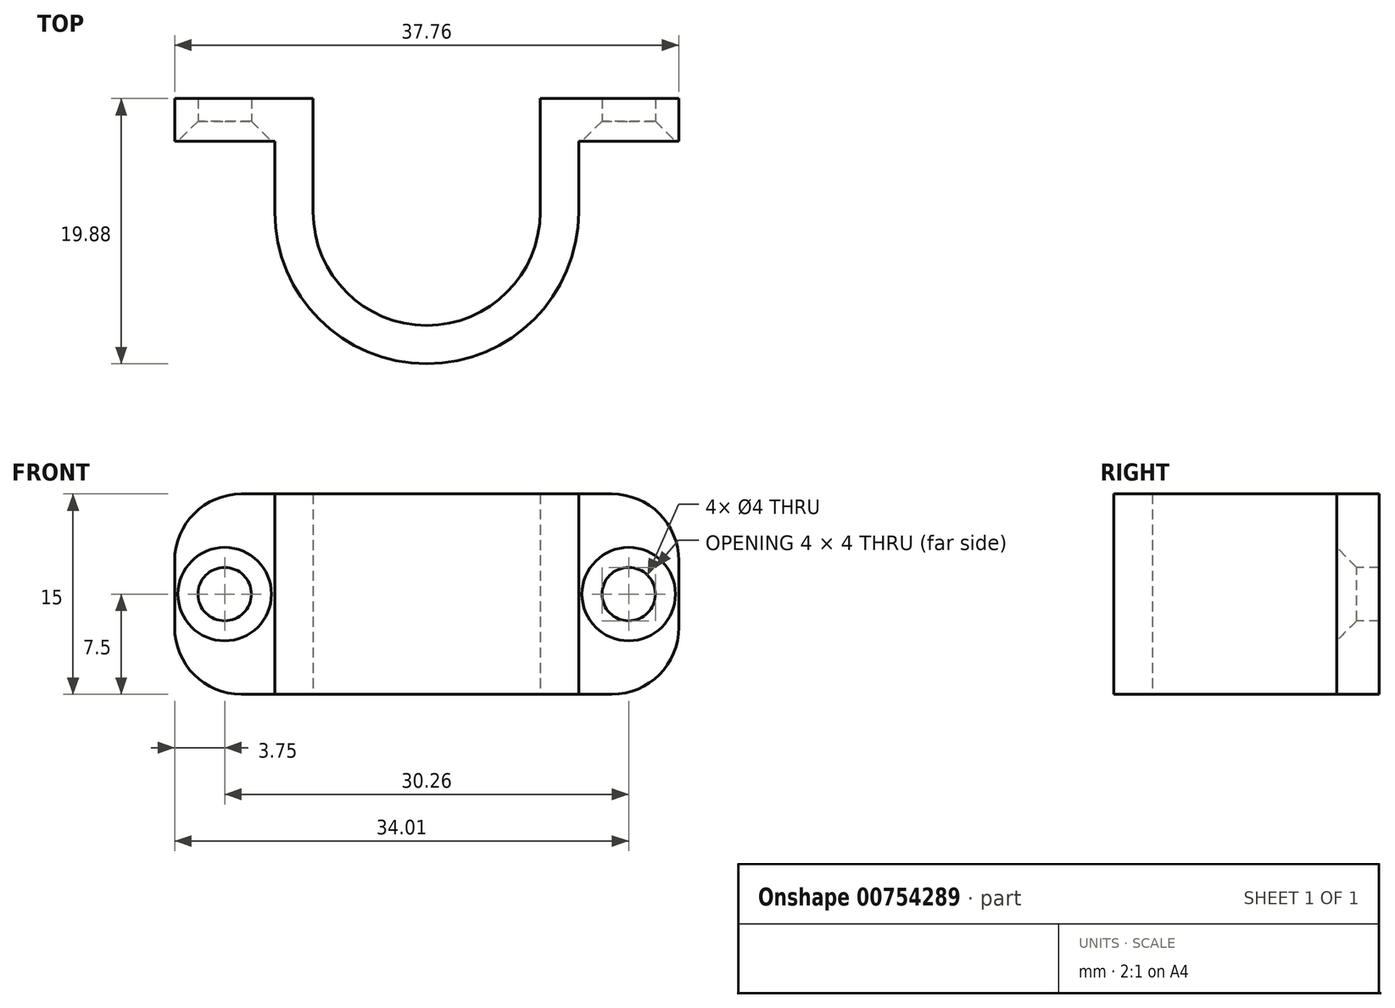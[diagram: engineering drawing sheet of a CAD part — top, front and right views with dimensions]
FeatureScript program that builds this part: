
annotation { "Feature Type Name" : "Feature", "Feature Type Description" : "" }
export const myFeature = defineFeature(function(context is Context, id is Id, definition is map)
    precondition{}
    {
        {
            var Q0;
            Q0=qCreatedBy(makeId("Top.planeOp"),FACE);
            var sketch = newSketch(context, id + "F0", { "sketchPlane" : qUnion([Q0])});
            skCircle(sketch, "E0", {"center": v(0, 0) * mm, "radius": 8.5 * mm});
            skLineSegment(sketch, "E1", {"start": v(-8.5, 0) * mm, "end": v(-8.5, 8.5) * mm});
            skLineSegment(sketch, "E2", {"start": v(-8.5, 8.5) * mm, "end": v(8.5, 8.5) * mm});
            skLineSegment(sketch, "E3", {"start": v(8.5, 8.5) * mm, "end": v(8.5, 0) * mm});
            skLineSegment(sketch, "E4.bottom", {"start": v(-8.5, 8.5) * mm, "end": v(-18.88, 8.5) * mm});
            skLineSegment(sketch, "E4.top", {"start": v(-8.5, 5.3) * mm, "end": v(-18.88, 5.3) * mm});
            skLineSegment(sketch, "E4.left", {"start": v(-8.5, 8.5) * mm, "end": v(-8.5, 5.3) * mm});
            skLineSegment(sketch, "E4.right", {"start": v(-18.88, 8.5) * mm, "end": v(-18.88, 5.3) * mm});
            skLineSegment(sketch, "E5", {"start": v(0, 0) * mm, "end": v(0, 27.69) * mm, "construction": true});
            skPoint(sketch, "E5.endSnap0", {"position": v(0, 8.5) * mm});
            skLineSegment(sketch, "E6.MirrorCS", {"start": v(8.5, 8.5) * mm, "end": v(8.5, 5.3) * mm});
            skLineSegment(sketch, "E7.MirrorCS", {"start": v(8.5, 5.3) * mm, "end": v(18.88, 5.3) * mm});
            skLineSegment(sketch, "E8.MirrorCS", {"start": v(8.5, 8.5) * mm, "end": v(18.88, 8.5) * mm});
            skLineSegment(sketch, "E9.MirrorCS", {"start": v(18.88, 8.5) * mm, "end": v(18.88, 5.3) * mm});
            skCircle(sketch, "E10", {"center": v(0, 0) * mm, "radius": 11.38 * mm});
            skLineSegment(sketch, "E11", {"start": v(-11.38, 0) * mm, "end": v(-11.38, 5.3) * mm});
            skLineSegment(sketch, "E12.MirrorCS", {"start": v(11.38, 0) * mm, "end": v(11.38, 5.3) * mm});
            skLineSegment(sketch, "E13", {"start": v(-8.5, 5.3) * mm, "end": v(8.5, 5.3) * mm});
            skSolve(sketch);
        }
        {
            var Q0;
            {var subQ4=sQuery(id+"F0.wireOp",EDGE,"E4.bottom");Q0=makeQuery(id+"F0.imprint","IMPRINT",FACE,{"disambiguationData":[TD([[makeQuery(id+"F0.imprint","IMPRINT",EDGE,{"derivedFrom":subQ4}),1.0]])]});}
            var Q1;
            {var subQ0=sQuery(id+"F0.wireOp",EDGE,"E11");Q1=makeQuery(id+"F0.imprint","IMPRINT",FACE,{"disambiguationData":[TD([[makeQuery(id+"F0.imprint","IMPRINT",EDGE,{"derivedFrom":subQ0}),-1.0]])]});}
            var Q2;
            {var subQ2=sQuery(id+"F0.wireOp",EDGE,"E1");var subQ9=sQuery(id+"F0.wireOp",EDGE,"E0");var subQ11=makeQuery(id+"F0.imprint","INTERSECT",VERTEX,{"derivedFrom":[subQ9,subQ2]});Q2=makeQuery(id+"F0.imprint","IMPRINT",FACE,{"disambiguationData":[TD([[makeQuery(id+"F0.imprint","IMPRINT",EDGE,{"disambiguationData":[TD([[subQ11,-1.0]])],"derivedFrom":subQ9}),-1.0]])]});}
            var Q3;
            {var subQ0=sQuery(id+"F0.wireOp",EDGE,"E12.MirrorCS");Q3=makeQuery(id+"F0.imprint","IMPRINT",FACE,{"disambiguationData":[TD([[makeQuery(id+"F0.imprint","IMPRINT",EDGE,{"derivedFrom":subQ0}),1.0]])]});}
            var Q4;
            {var subQ0=sQuery(id+"F0.wireOp",EDGE,"E8.MirrorCS");Q4=makeQuery(id+"F0.imprint","IMPRINT",FACE,{"disambiguationData":[TD([[makeQuery(id+"F0.imprint","IMPRINT",EDGE,{"derivedFrom":subQ0}),-1.0]])]});}
            var Q5;
            {var subQ2=sQuery(id+"F0.wireOp",EDGE,"E1");var subQ9=sQuery(id+"F0.wireOp",EDGE,"E0");var subQ11=makeQuery(id+"F0.imprint","INTERSECT",VERTEX,{"derivedFrom":[subQ9,subQ2]});Q5=makeQuery(id+"F0.imprint","IMPRINT",FACE,{"disambiguationData":[TD([[makeQuery(id+"F0.imprint","IMPRINT",EDGE,{"disambiguationData":[TD([[subQ11,-1.0]])],"derivedFrom":subQ9}),-1.0]])]});}
            var Q6;
            {var subQ1=sQuery(id+"F0.wireOp",EDGE,"E1");var subQ3=sQuery(id+"F0.wireOp",EDGE,"E10");var subQ4=makeQuery(id+"F0.imprint","INTERSECT",VERTEX,{"derivedFrom":[subQ1,subQ3]});Q6=makeQuery(id+"F0.imprint","IMPRINT",FACE,{"disambiguationData":[TD([[makeQuery(id+"F0.imprint","IMPRINT",EDGE,{"disambiguationData":[TD([[subQ4,-1.0]])],"derivedFrom":subQ3}),1.0]])]});}
            var Q7;
            {var subQ1=sQuery(id+"F0.wireOp",EDGE,"E3");var subQ3=sQuery(id+"F0.wireOp",EDGE,"E10");var subQ4=makeQuery(id+"F0.imprint","INTERSECT",VERTEX,{"derivedFrom":[subQ1,subQ3]});Q7=makeQuery(id+"F0.imprint","IMPRINT",FACE,{"disambiguationData":[TD([[makeQuery(id+"F0.imprint","IMPRINT",EDGE,{"disambiguationData":[TD([[subQ4,1.0]])],"derivedFrom":subQ3}),1.0]])]});}
            extrude(context, id + "F1", {"entities" : qUnion([Q0, Q1, Q2, Q3, Q4, Q5, Q6, Q7]), "depth" : 15 * mm, "offsetDistance" : 25 * mm});
        }
        {
            var Q0;
            Q0=makeQuery(id+"F1.opExtrude","SWEPT_FACE",FACE,{"disambiguationData":[OSD([sQuery(id+"F0.wireOp",EDGE,"E4.top")])]});
            var sketch = newSketch(context, id + "F2", { "sketchPlane" : qUnion([Q0])});
            skLineSegment(sketch, "E14", {"start": v(-11.38, 0) * mm, "end": v(-18.88, 15) * mm, "construction": true});
            skLineSegment(sketch, "E15", {"start": v(-18.88, 0) * mm, "end": v(-11.38, 15) * mm, "construction": true});
            skCircle(sketch, "E16", {"center": v(-15.13, 7.5) * mm, "radius": 2.5 * mm});
            skLineSegment(sketch, "E17", {"start": v(0, 0) * mm, "end": v(0, 26.07) * mm, "construction": true});
            skCircle(sketch, "E18.MirrorC", {"center": v(15.13, 7.5) * mm, "radius": 2.5 * mm});
            skLineSegment(sketch, "E19.MirrorCS", {"start": v(11.38, 0) * mm, "end": v(18.88, 15) * mm, "construction": true});
            skLineSegment(sketch, "E20.MirrorCS", {"start": v(18.88, 0) * mm, "end": v(11.38, 15) * mm, "construction": true});
            skSolve(sketch);
        }
        {
            var Q0;
            Q0=sQuery(id+"F2.wireOp",VERTEX,"E16.center");
            var Q1;
            Q1=sQuery(id+"F2.wireOp",VERTEX,"E18.MirrorC.center");
            var Q2;
            Q2=makeQuery(id+"F1.opExtrude","SWEPT_BODY",BODY,{"disambiguationData":[OSD([sQuery(id+"F0.wireOp",EDGE,"E0"),sQuery(id+"F0.wireOp",EDGE,"E1"),sQuery(id+"F0.wireOp",EDGE,"E3"),sQuery(id+"F0.wireOp",EDGE,"E4.bottom"),sQuery(id+"F0.wireOp",EDGE,"E4.top"),sQuery(id+"F0.wireOp",EDGE,"E4.right"),sQuery(id+"F0.wireOp",EDGE,"E7.MirrorCS"),sQuery(id+"F0.wireOp",EDGE,"E8.MirrorCS"),sQuery(id+"F0.wireOp",EDGE,"E9.MirrorCS"),sQuery(id+"F0.wireOp",EDGE,"E10"),sQuery(id+"F0.wireOp",EDGE,"E11"),sQuery(id+"F0.wireOp",EDGE,"E12.MirrorCS")])]});
            hole(context, id + "F3", {"style" : HoleStyle.C_SINK, "endStyle" : HoleEndStyle.THROUGH, "holeDiameter" : 4 * mm, "cSinkDiameter" : 7 * mm, "cSinkAngle" : 90 * degree, "majorDiameter" : 5 * mm, "isTappedThrough" : true, "tappedDepth" : 12 * mm, "tapClearance" : 3, "startFromSketch" : true, "locations" : qUnion([Q0, Q1]), "scope" : qUnion([Q2])});
        }
        {
            var Q0;
            Q0=makeQuery(id+"F1.opExtrude","CAP_EDGE",EDGE,{"disambiguationData":[OSD([sQuery(id+"F0.wireOp",EDGE,"E4.right")])],"isStart":false});
            var Q1;
            Q1=makeQuery(id+"F1.opExtrude","CAP_EDGE",EDGE,{"disambiguationData":[OSD([sQuery(id+"F0.wireOp",EDGE,"E4.right")])],"isStart":true});
            var Q2;
            Q2=makeQuery(id+"F1.opExtrude","CAP_EDGE",EDGE,{"disambiguationData":[OSD([sQuery(id+"F0.wireOp",EDGE,"E9.MirrorCS")])],"isStart":false});
            var Q3;
            Q3=makeQuery(id+"F1.opExtrude","CAP_EDGE",EDGE,{"disambiguationData":[OSD([sQuery(id+"F0.wireOp",EDGE,"E9.MirrorCS")])],"isStart":true});
            fillet(context, id + "F4", {"entities" : qUnion([Q0, Q1, Q2, Q3]), "radius" : 5 * mm, "tangentPropagation" : true, "allowEdgeOverflow" : false});
        }
    });
